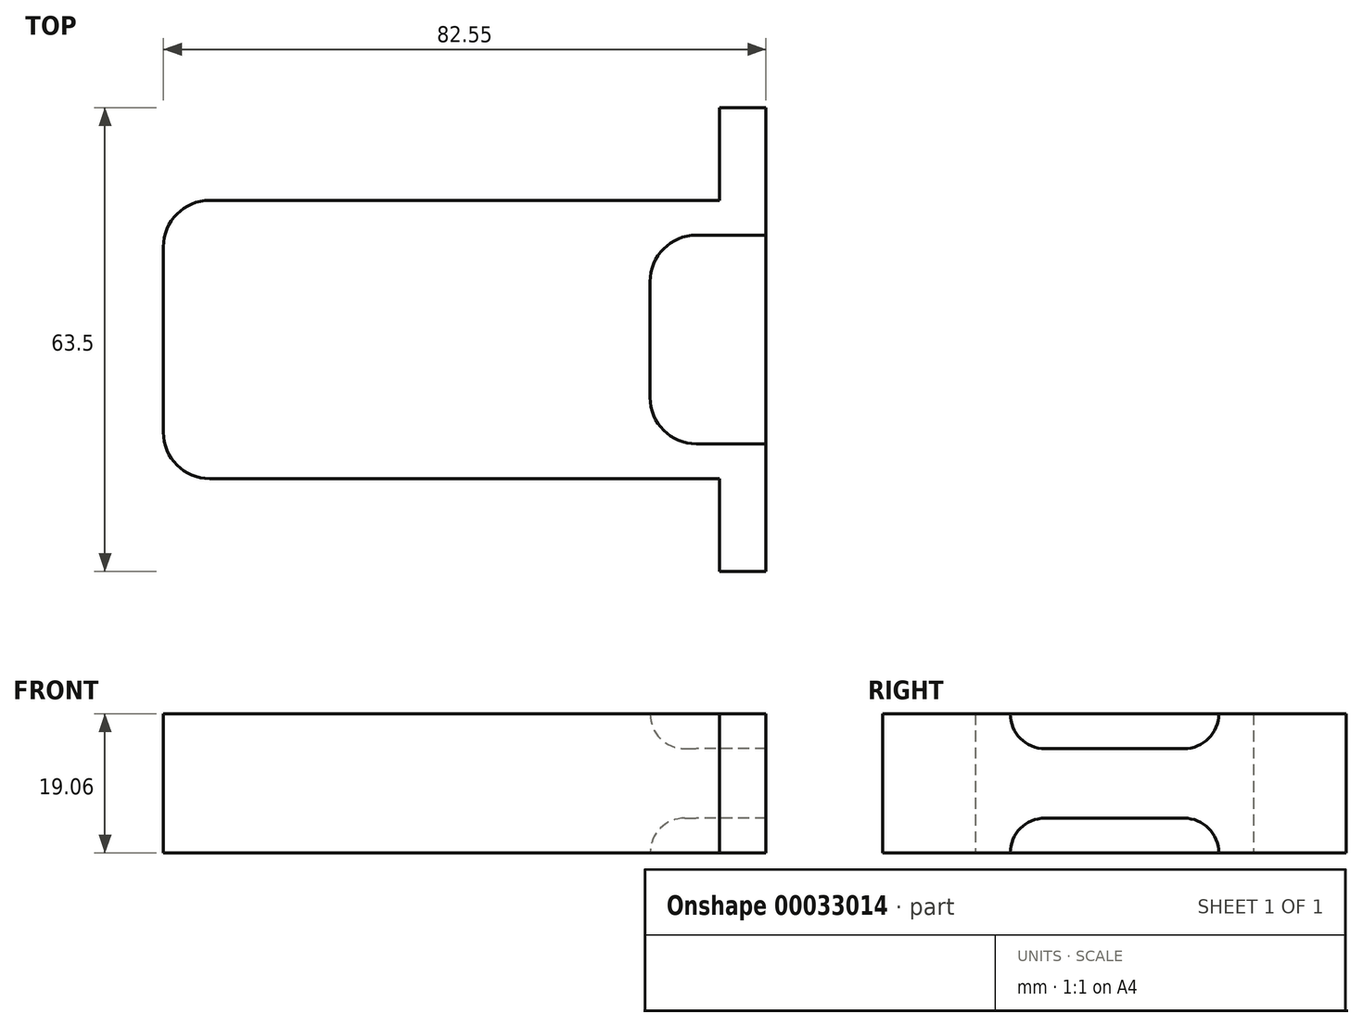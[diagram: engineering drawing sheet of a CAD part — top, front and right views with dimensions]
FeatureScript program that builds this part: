
annotation { "Feature Type Name" : "Feature", "Feature Type Description" : "" }
export const myFeature = defineFeature(function(context is Context, id is Id, definition is map)
    precondition{}
    {
        {
            var Q0;
            Q0=qCreatedBy(makeId("Top.planeOp"),FACE);
            var sketch = newSketch(context, id + "F0", { "sketchPlane" : qUnion([Q0])});
            skLineSegment(sketch, "E0", {"start": v(-82.55, -19.05) * mm, "end": v(-6.35, -19.05) * mm});
            skLineSegment(sketch, "E1", {"start": v(-6.35, -19.05) * mm, "end": v(-6.35, -31.75) * mm});
            skLineSegment(sketch, "E2", {"start": v(-6.35, -31.75) * mm, "end": v(0, -31.75) * mm});
            skLineSegment(sketch, "E3", {"start": v(0, -31.75) * mm, "end": v(0, 31.75) * mm});
            skLineSegment(sketch, "E4", {"start": v(0, 31.75) * mm, "end": v(-6.35, 31.75) * mm});
            skLineSegment(sketch, "E5", {"start": v(-6.35, 31.75) * mm, "end": v(-6.35, 19.05) * mm});
            skLineSegment(sketch, "E6", {"start": v(-6.35, 19.05) * mm, "end": v(-82.55, 19.05) * mm});
            skLineSegment(sketch, "E7", {"start": v(-82.55, 19.05) * mm, "end": v(-82.55, -19.05) * mm});
            skSolve(sketch);
        }
        {
            var Q0;
            Q0=makeQuery(id+"F0.imprint","IMPRINT",FACE,{"disambiguationData":[TD([[makeQuery(id+"F0.imprint","IMPRINT",EDGE,{"derivedFrom":sQuery(id+"F0.wireOp",EDGE,"E0")}),1.0]])]});
            extrude(context, id + "F1", {"entities" : qUnion([Q0]), "endBound" : BoundingType.SYMMETRIC, "depth" : 19.05 * mm});
        }
        {
            var Q0;
            Q0=makeQuery(id+"F1.opExtrude","SWEPT_EDGE",EDGE,{"disambiguationData":[OSD([sQuery(id+"F0.wireOp",EDGE,"E0"),sQuery(id+"F0.wireOp",EDGE,"E7")])]});
            var Q1;
            Q1=makeQuery(id+"F1.opExtrude","SWEPT_EDGE",EDGE,{"disambiguationData":[OSD([sQuery(id+"F0.wireOp",EDGE,"E6"),sQuery(id+"F0.wireOp",EDGE,"E7")])]});
            fillet(context, id + "F2", {"entities" : qUnion([Q0, Q1]), "radius" : 6.35 * mm, "tangentPropagation" : true, "allowEdgeOverflow" : false});
        }
        {
            var Q0;
            Q0=makeQuery(id+"F1.opExtrude","CAP_FACE",FACE,{"disambiguationData":[OSD([sQuery(id+"F0.wireOp",EDGE,"E0"),sQuery(id+"F0.wireOp",EDGE,"E1"),sQuery(id+"F0.wireOp",EDGE,"E2"),sQuery(id+"F0.wireOp",EDGE,"E3"),sQuery(id+"F0.wireOp",EDGE,"E4"),sQuery(id+"F0.wireOp",EDGE,"E5"),sQuery(id+"F0.wireOp",EDGE,"E6"),sQuery(id+"F0.wireOp",EDGE,"E7")])],"isStart":false});
            var sketch = newSketch(context, id + "F3", { "sketchPlane" : qUnion([Q0])});
            skLineSegment(sketch, "E8.bottom", {"start": v(0, 14.29) * mm, "end": v(-9.53, 14.29) * mm});
            skLineSegment(sketch, "E8.top", {"start": v(0, -14.29) * mm, "end": v(-9.52, -14.29) * mm});
            skLineSegment(sketch, "E8.left", {"start": v(0, 14.29) * mm, "end": v(0, -14.29) * mm});
            skLineSegment(sketch, "E8.right", {"start": v(-15.88, 7.94) * mm, "end": v(-15.87, -7.94) * mm});
            skPoint(sketch, "E9.visualSharp", {"position": v(-15.88, 14.29) * mm});
            skArc(sketch, "E9.filletArc", {"start": v(-9.53, 14.29) * mm, "mid": v(-14.02, 12.43) * mm, "end": v(-15.88, 7.94) * mm});
            skPoint(sketch, "E10.visualSharp", {"position": v(-15.87, -14.29) * mm});
            skArc(sketch, "E10.filletArc", {"start": v(-15.88, -7.94) * mm, "mid": v(-14.02, -12.43) * mm, "end": v(-9.52, -14.29) * mm});
            skSolve(sketch);
        }
        {
            var Q0;
            Q0=makeQuery(id+"F3.imprint","IMPRINT",FACE,{"disambiguationData":[TD([[makeQuery(id+"F3.imprint","IMPRINT",EDGE,{"derivedFrom":sQuery(id+"F3.wireOp",EDGE,"E8.bottom")}),1.0]])]});
            extrude(context, id + "F4", {"entities" : qUnion([Q0]), "operationType" : NewBodyOperationType.REMOVE, "oppositeDirection" : true, "depth" : 4.76 * mm});
        }
        {
            var Q0;
            Q0=makeQuery(id+"F4.boolean.opBoolean","COPY",EDGE,{"derivedFrom":makeQuery(id+"F4.opExtrude","CAP_EDGE",EDGE,{"disambiguationData":[OSD([sQuery(id+"F3.wireOp",EDGE,"E8.bottom")])],"isStart":false})});
            var Q1;
            Q1=makeQuery(id+"F4.boolean.opBoolean","COPY",EDGE,{"derivedFrom":makeQuery(id+"F4.opExtrude","CAP_EDGE",EDGE,{"disambiguationData":[OSD([sQuery(id+"F3.wireOp",EDGE,"E9.filletArc")])],"isStart":false})});
            fillet(context, id + "F5", {"entities" : qUnion([Q0, Q1]), "radius" : 4.76 * mm, "tangentPropagation" : true, "allowEdgeOverflow" : false});
        }
        {
            var Q0;
            Q0=makeQuery(id+"F1.opExtrude","CAP_FACE",FACE,{"disambiguationData":[OSD([sQuery(id+"F0.wireOp",EDGE,"E0"),sQuery(id+"F0.wireOp",EDGE,"E1"),sQuery(id+"F0.wireOp",EDGE,"E2"),sQuery(id+"F0.wireOp",EDGE,"E3"),sQuery(id+"F0.wireOp",EDGE,"E4"),sQuery(id+"F0.wireOp",EDGE,"E5"),sQuery(id+"F0.wireOp",EDGE,"E6"),sQuery(id+"F0.wireOp",EDGE,"E7")])],"isStart":true});
            var sketch = newSketch(context, id + "F6", { "sketchPlane" : qUnion([Q0])});
            skLineSegment(sketch, "E11.bottom", {"start": v(9.51, 14.29) * mm, "end": v(-9.53, 14.29) * mm});
            skLineSegment(sketch, "E11.top", {"start": v(9.51, -14.29) * mm, "end": v(-9.52, -14.29) * mm});
            skLineSegment(sketch, "E11.left", {"start": v(9.51, 14.29) * mm, "end": v(9.51, -14.29) * mm});
            skLineSegment(sketch, "E11.right", {"start": v(-15.88, 7.94) * mm, "end": v(-15.88, -7.94) * mm});
            skPoint(sketch, "E12.visualSharp", {"position": v(-15.88, 14.29) * mm});
            skArc(sketch, "E12.filletArc", {"start": v(-9.53, 14.29) * mm, "mid": v(-14.02, 12.43) * mm, "end": v(-15.88, 7.94) * mm});
            skPoint(sketch, "E13.visualSharp", {"position": v(-15.87, -14.29) * mm});
            skArc(sketch, "E13.filletArc", {"start": v(-15.87, -7.94) * mm, "mid": v(-14.02, -12.43) * mm, "end": v(-9.52, -14.29) * mm});
            skSolve(sketch);
        }
        {
            var Q0;
            Q0=makeQuery(id+"F6.imprint","IMPRINT",FACE,{"disambiguationData":[TD([[makeQuery(id+"F6.imprint","IMPRINT",EDGE,{"derivedFrom":sQuery(id+"F6.wireOp",EDGE,"E11.right")}),1.0]])]});
            extrude(context, id + "F7", {"entities" : qUnion([Q0]), "operationType" : NewBodyOperationType.REMOVE, "oppositeDirection" : true, "depth" : 4.76 * mm});
        }
        {
            var Q0;
            Q0=makeQuery(id+"F7.boolean.opBoolean","COPY",EDGE,{"derivedFrom":makeQuery(id+"F7.opExtrude","CAP_EDGE",EDGE,{"disambiguationData":[OSD([sQuery(id+"F6.wireOp",EDGE,"E11.bottom")])],"isStart":false})});
            var Q1;
            Q1=makeQuery(id+"F7.boolean.opBoolean","COPY",EDGE,{"derivedFrom":makeQuery(id+"F7.opExtrude","CAP_EDGE",EDGE,{"disambiguationData":[OSD([sQuery(id+"F6.wireOp",EDGE,"E12.filletArc")])],"isStart":false})});
            fillet(context, id + "F8", {"entities" : qUnion([Q0, Q1]), "radius" : 4.76 * mm, "tangentPropagation" : true, "allowEdgeOverflow" : false});
        }
    });
